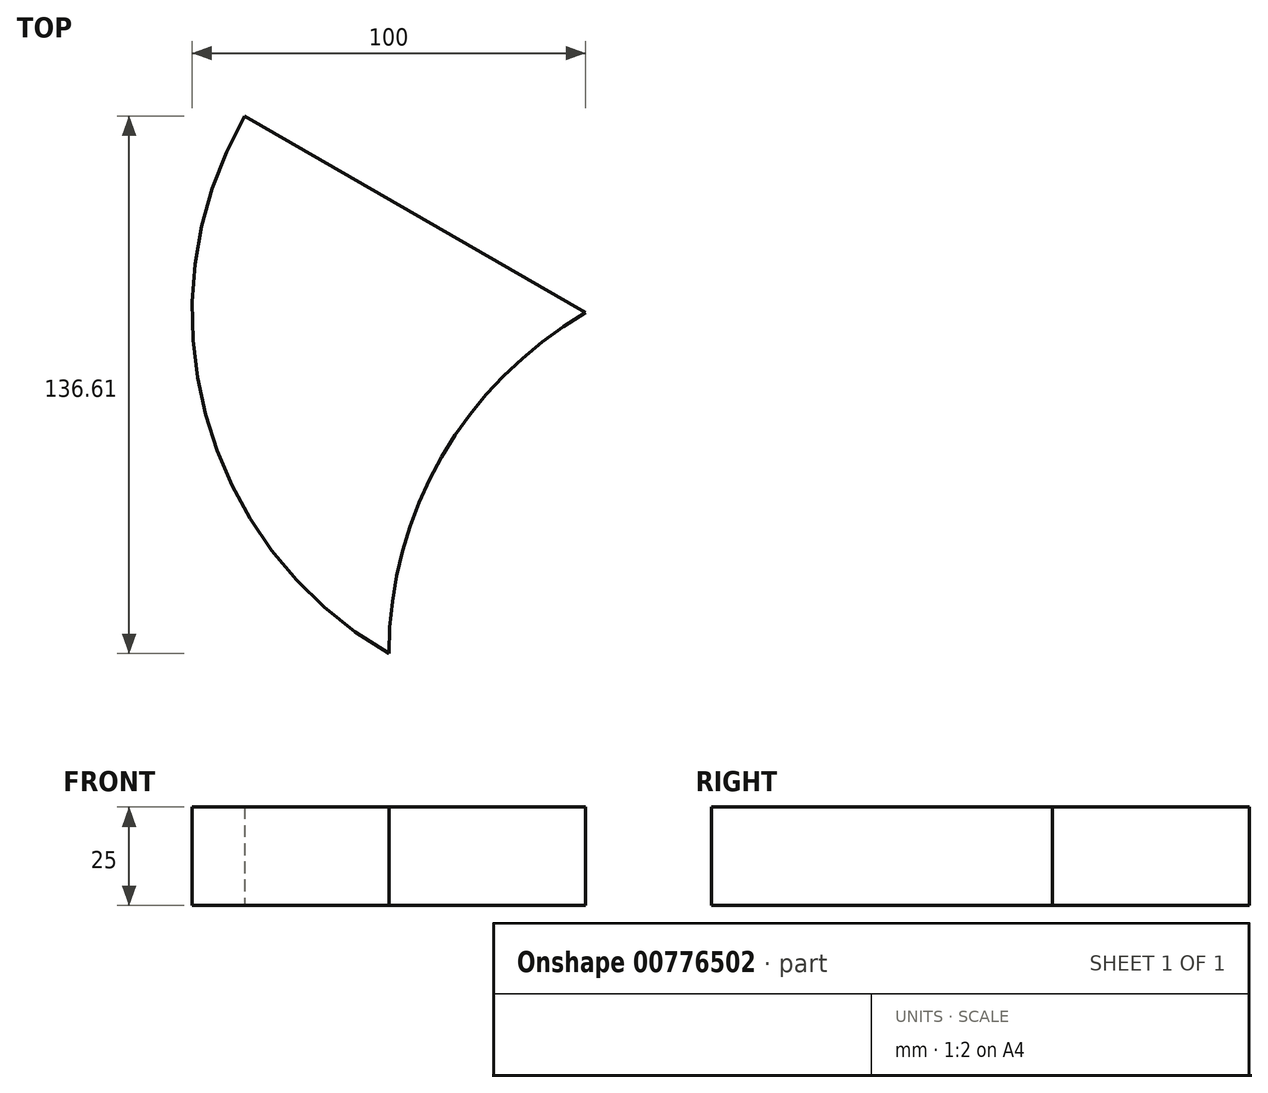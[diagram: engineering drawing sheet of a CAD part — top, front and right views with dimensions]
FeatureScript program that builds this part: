
annotation { "Feature Type Name" : "Feature", "Feature Type Description" : "" }
export const myFeature = defineFeature(function(context is Context, id is Id, definition is map)
    precondition{}
    {
        {
            var Q0;
            Q0=qCreatedBy(makeId("Top.planeOp"),FACE);
            var sketch = newSketch(context, id + "F0", { "sketchPlane" : qUnion([Q0])});
            skLineSegment(sketch, "E0", {"start": v(-50, -28.87) * mm, "end": v(0, 57.74) * mm, "construction": true});
            skLineSegment(sketch, "E1", {"start": v(0, 57.74) * mm, "end": v(50, -28.87) * mm, "construction": true});
            skLineSegment(sketch, "E2", {"start": v(50, -28.87) * mm, "end": v(-50, -28.87) * mm, "construction": true});
            skLineSegment(sketch, "E3", {"start": v(0, 57.74) * mm, "end": v(0, 0) * mm, "construction": true});
            skArc(sketch, "E4", {"start": v(86.6, 7.74) * mm, "mid": v(-50, -28.87) * mm, "end": v(-86.6, 107.74) * mm});
            skLineSegment(sketch, "E5", {"start": v(0, 0) * mm, "end": v(50, -28.87) * mm, "construction": true});
            skLineSegment(sketch, "E6", {"start": v(0, 0) * mm, "end": v(-50, -28.87) * mm, "construction": true});
            skLineSegment(sketch, "E7", {"start": v(0, 0) * mm, "end": v(0, -76.9) * mm, "construction": true});
            skLineSegment(sketch, "E8", {"start": v(0, 0) * mm, "end": v(0, -76.9) * mm});
            skLineSegment(sketch, "E9", {"start": v(-86.6, 107.74) * mm, "end": v(86.6, 7.74) * mm});
            skArc(sketch, "E10", {"start": v(-50, -28.87) * mm, "mid": v(-36.6, 21.13) * mm, "end": v(0, 57.74) * mm});
            skArc(sketch, "E11", {"start": v(0, 57.74) * mm, "mid": v(36.6, 21.13) * mm, "end": v(50, -28.87) * mm});
            skSolve(sketch);
        }
        {
            var Q0;
            {var subQ0=sQuery(id+"F0.wireOp",EDGE,"E9");Q0=makeQuery(id+"F0.imprint","IMPRINT",FACE,{"disambiguationData":[TD([[makeQuery(id+"F0.imprint","IMPRINT",EDGE,{"derivedFrom":subQ0}),-1.0]])]});}
            var Q1;
            {var subQ0=sQuery(id+"F0.wireOp",EDGE,"E10");Q1=makeQuery(id+"F0.imprint","IMPRINT",FACE,{"disambiguationData":[TD([[makeQuery(id+"F0.imprint","IMPRINT",EDGE,{"derivedFrom":subQ0}),-1.0]])]});}
            var Q2;
            Q2=sQuery(id+"F0.wireOp",EDGE,"E9");
            revolve(context, id + "F1", {"surfaceOperationType" : NewSurfaceOperationType.NEW, "entities" : qUnion([Q0, Q1]), "axis" : qUnion([Q2]), "revolveType" : RevolveType.FULL});
        }
        {
            var Q0;
            Q0=qCreatedBy(makeId("Right.planeOp"),FACE);
            var sketch = newSketch(context, id + "F2", { "sketchPlane" : qUnion([Q0])});
            skLineSegment(sketch, "E12", {"start": v(-28.87, 0) * mm, "end": v(0, 81.65) * mm, "construction": true});
            skLineSegment(sketch, "E13", {"start": v(0, 81.65) * mm, "end": v(57.74, 0) * mm, "construction": true});
            skLineSegment(sketch, "E14", {"start": v(57.74, 0) * mm, "end": v(-28.87, 0) * mm, "construction": true});
            skSolve(sketch);
        }
        {
            var Q0;
            Q0=makeQuery(id+"F1.opRevolve","SWEPT_BODY",BODY,{"disambiguationData":[OSD([sQuery(id+"F0.wireOp",EDGE,"E4"),sQuery(id+"F0.wireOp",EDGE,"E9")])]});
            var Q1;
            Q1=sQuery(id+"F0.wireOp",EDGE,"E1");
            transform(context, id + "F3", {"entities" : qUnion([Q0]), "transformType" : TransformType.TRANSLATION_ENTITY, "oppositeDirectionEntity" : false, "transformLine" : qUnion([Q1]), "makeCopy" : true});
        }
        {
            var Q0;
            Q0=makeQuery(id+"F1.opRevolve","SWEPT_BODY",BODY,{"disambiguationData":[OSD([sQuery(id+"F0.wireOp",EDGE,"E4"),sQuery(id+"F0.wireOp",EDGE,"E9")])]});
            var Q1;
            Q1=sQuery(id+"F0.wireOp",EDGE,"E0");
            transform(context, id + "F4", {"entities" : qUnion([Q0]), "transformType" : TransformType.TRANSLATION_ENTITY, "oppositeDirectionEntity" : true, "transformLine" : qUnion([Q1]), "makeCopy" : true});
        }
        {
            var Q0;
            Q0=makeQuery(id+"F1.opRevolve","SWEPT_BODY",BODY,{"disambiguationData":[OSD([sQuery(id+"F0.wireOp",EDGE,"E4"),sQuery(id+"F0.wireOp",EDGE,"E9")])]});
            var Q1;
            Q1=sQuery(id+"F2.wireOp",EDGE,"E13");
            transform(context, id + "F5", {"entities" : qUnion([Q0]), "transformType" : TransformType.TRANSLATION_ENTITY, "oppositeDirectionEntity" : true, "transformLine" : qUnion([Q1]), "makeCopy" : true});
        }
        {
            var Q0;
            Q0=makeQuery(id+"F5.opPattern","COPY",BODY,{"derivedFrom":makeQuery(id+"F1.opRevolve","SWEPT_BODY",BODY,{"disambiguationData":[OSD([sQuery(id+"F0.wireOp",EDGE,"E4"),sQuery(id+"F0.wireOp",EDGE,"E9")])]}),"instanceName":"1"});
            var Q1;
            Q1=makeQuery(id+"F3.opPattern","COPY",BODY,{"derivedFrom":makeQuery(id+"F1.opRevolve","SWEPT_BODY",BODY,{"disambiguationData":[OSD([sQuery(id+"F0.wireOp",EDGE,"E4"),sQuery(id+"F0.wireOp",EDGE,"E9")])]}),"instanceName":"1"});
            var Q2;
            Q2=makeQuery(id+"F4.opPattern","COPY",BODY,{"derivedFrom":makeQuery(id+"F1.opRevolve","SWEPT_BODY",BODY,{"disambiguationData":[OSD([sQuery(id+"F0.wireOp",EDGE,"E4"),sQuery(id+"F0.wireOp",EDGE,"E9")])]}),"instanceName":"1"});
            var Q3;
            Q3=makeQuery(id+"F1.opRevolve","SWEPT_BODY",BODY,{"disambiguationData":[OSD([sQuery(id+"F0.wireOp",EDGE,"E4"),sQuery(id+"F0.wireOp",EDGE,"E9")])]});
            booleanBodies(context, id + "F6", {"operationType" : BooleanOperationType.INTERSECTION, "tools" : qUnion([Q0, Q1, Q2, Q3])});
        }
        {
            var Q0;
            {var subQ0=sQuery(id+"F0.wireOp",EDGE,"E10");Q0=makeQuery(id+"F0.imprint","IMPRINT",FACE,{"disambiguationData":[TD([[makeQuery(id+"F0.imprint","IMPRINT",EDGE,{"derivedFrom":subQ0}),-1.0]])]});}
            extrude(context, id + "F7", {"entities" : qUnion([Q0]), "depth" : 25 * mm, "offsetDistance" : 25 * mm});
        }
    });
